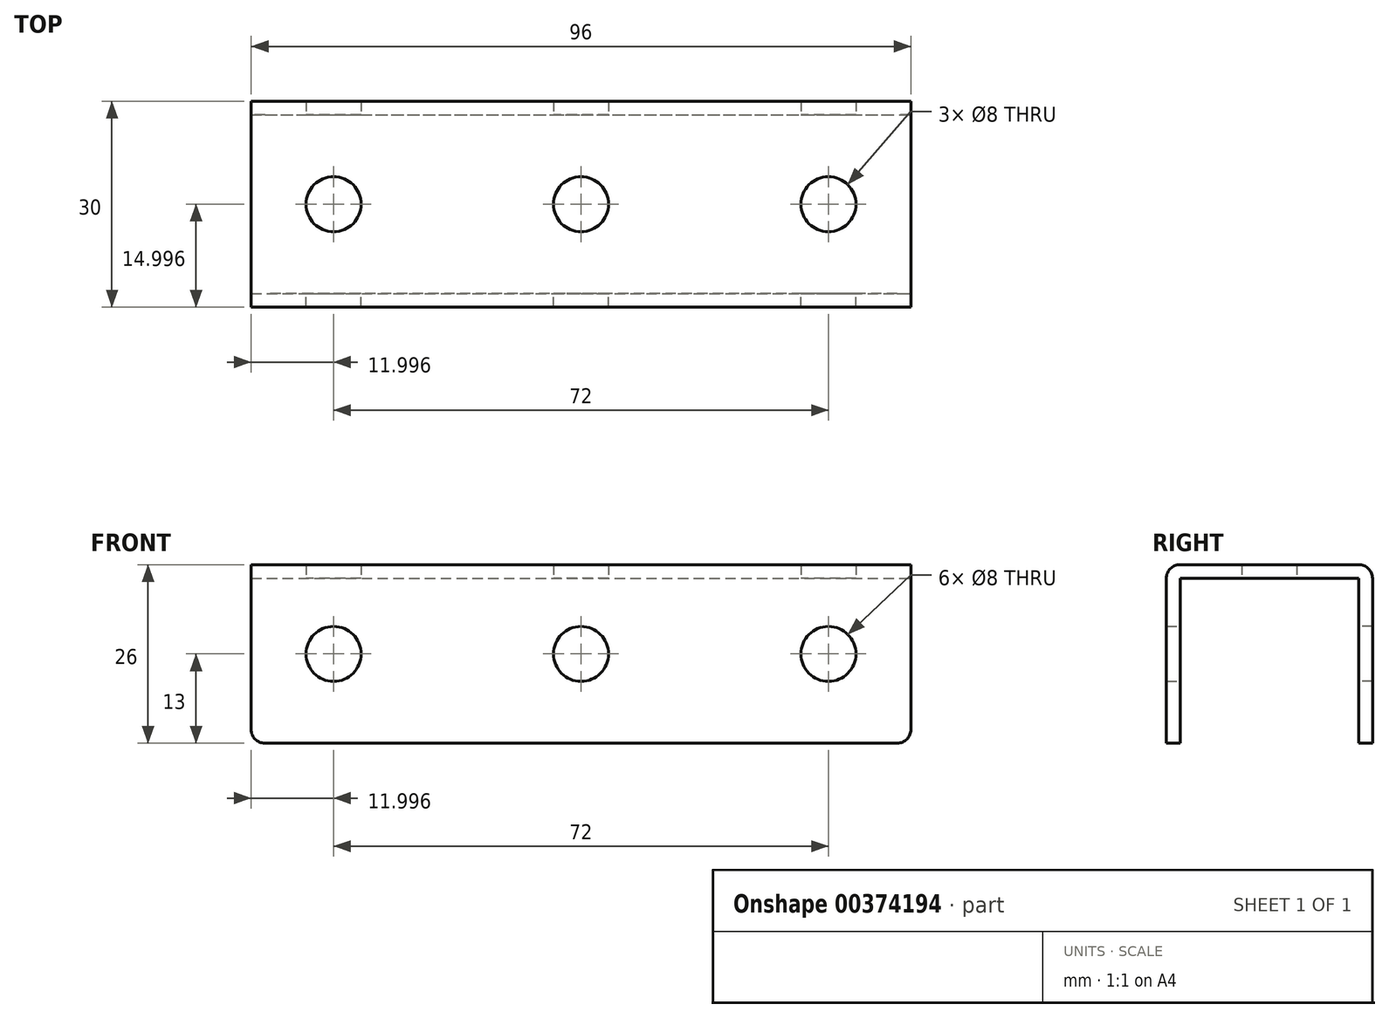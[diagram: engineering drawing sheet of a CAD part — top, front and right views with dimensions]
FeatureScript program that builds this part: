
annotation { "Feature Type Name" : "Feature", "Feature Type Description" : "" }
export const myFeature = defineFeature(function(context is Context, id is Id, definition is map)
    precondition{}
    {
        {
            var Q0;
            Q0=qCreatedBy(makeId("Top.planeOp"),FACE);
            var sketch = newSketch(context, id + "F0", { "sketchPlane" : qUnion([Q0])});
            skLineSegment(sketch, "E0.bottom", {"start": v(-30.68, 13.97) * mm, "end": v(65.32, 13.97) * mm});
            skLineSegment(sketch, "E0.top", {"start": v(-30.68, -12.03) * mm, "end": v(65.32, -12.03) * mm});
            skLineSegment(sketch, "E0.left", {"start": v(-30.68, 13.97) * mm, "end": v(-30.68, -12.03) * mm});
            skLineSegment(sketch, "E0.right", {"start": v(65.32, 13.97) * mm, "end": v(65.32, -12.03) * mm});
            skLineSegment(sketch, "E1", {"start": v(17.32, 13.97) * mm, "end": v(17.32, -12.03) * mm, "construction": true});
            skLineSegment(sketch, "E2", {"start": v(53.32, 13.97) * mm, "end": v(53.32, -12.03) * mm, "construction": true});
            skLineSegment(sketch, "E3", {"start": v(-18.68, 13.97) * mm, "end": v(-18.68, -12.03) * mm, "construction": true});
            skCircle(sketch, "E4", {"center": v(17.32, 0.97) * mm, "radius": 4 * mm});
            skCircle(sketch, "E5", {"center": v(53.32, 0.97) * mm, "radius": 4 * mm});
            skCircle(sketch, "E6", {"center": v(-18.68, 0.97) * mm, "radius": 4 * mm});
            skSolve(sketch);
        }
        {
            var Q0;
            Q0=makeQuery(id+"F0.imprint","IMPRINT",FACE,{"disambiguationData":[TD([[makeQuery(id+"F0.imprint","IMPRINT",EDGE,{"derivedFrom":sQuery(id+"F0.wireOp",EDGE,"E0.bottom")}),-1.0]])]});
            extrude(context, id + "F1", {"entities" : qUnion([Q0]), "depth" : 2 * mm});
        }
        {
            var Q0;
            Q0=makeQuery(id+"F1.opExtrude","SWEPT_FACE",FACE,{"disambiguationData":[OSD([sQuery(id+"F0.wireOp",EDGE,"E0.bottom")])]});
            cPlane(context, id + "F2", {"entities" : qUnion([Q0]), "cplaneType" : CPlaneType.OFFSET, "offset" : 0 * mm, "width" : 150 * mm, "height" : 150 * mm});
        }
        {
            var Q0;
            Q0=makeQuery(id+"F1.opExtrude","SWEPT_FACE",FACE,{"disambiguationData":[OSD([sQuery(id+"F0.wireOp",EDGE,"E0.top")])]});
            cPlane(context, id + "F3", {"entities" : qUnion([Q0]), "cplaneType" : CPlaneType.OFFSET, "offset" : 0 * mm, "width" : 150 * mm, "height" : 150 * mm});
        }
        {
            var Q0;
            Q0=qCreatedBy(id+"F2.planeOp",FACE);
            var sketch = newSketch(context, id + "F4", { "sketchPlane" : qUnion([Q0])});
            skLineSegment(sketch, "E7.0", {"start": v(30.68, 2) * mm, "end": v(-65.32, 2) * mm});
            skLineSegment(sketch, "E8", {"start": v(-65.32, 2) * mm, "end": v(-65.32, -24) * mm});
            skLineSegment(sketch, "E9", {"start": v(30.68, 2) * mm, "end": v(30.68, -24) * mm});
            skLineSegment(sketch, "E10", {"start": v(30.68, -24) * mm, "end": v(-65.32, -24) * mm});
            skLineSegment(sketch, "E11", {"start": v(-53.32, 2) * mm, "end": v(-53.32, -24) * mm, "construction": true});
            skLineSegment(sketch, "E12", {"start": v(18.68, 2) * mm, "end": v(18.68, -24) * mm, "construction": true});
            skLineSegment(sketch, "E13", {"start": v(-17.32, 2) * mm, "end": v(-17.32, -24) * mm, "construction": true});
            skCircle(sketch, "E14", {"center": v(-17.32, -11) * mm, "radius": 4 * mm});
            skCircle(sketch, "E15", {"center": v(18.68, -11) * mm, "radius": 4 * mm});
            skCircle(sketch, "E16", {"center": v(-53.32, -11) * mm, "radius": 4 * mm});
            skSolve(sketch);
        }
        {
            var Q0;
            Q0=qCreatedBy(id+"F3.planeOp",FACE);
            var sketch = newSketch(context, id + "F5", { "sketchPlane" : qUnion([Q0])});
            skLineSegment(sketch, "E17.0.0", {"start": v(65.32, -24) * mm, "end": v(-30.68, -24) * mm});
            skLineSegment(sketch, "E17.0.1", {"start": v(-30.68, -24) * mm, "end": v(-30.68, 2) * mm});
            skLineSegment(sketch, "E17.0.2", {"start": v(-30.68, 2) * mm, "end": v(65.32, 2) * mm});
            skLineSegment(sketch, "E17.0.3", {"start": v(65.32, 2) * mm, "end": v(65.32, -24) * mm});
            skCircle(sketch, "E18.0", {"center": v(-18.68, -11) * mm, "radius": 4 * mm});
            skCircle(sketch, "E19.0", {"center": v(17.32, -11) * mm, "radius": 4 * mm});
            skCircle(sketch, "E20.0", {"center": v(53.32, -11) * mm, "radius": 4 * mm});
            skSolve(sketch);
        }
        {
            var Q0;
            Q0=makeQuery(id+"F5.imprint","IMPRINT",FACE,{"disambiguationData":[TD([[makeQuery(id+"F5.imprint","IMPRINT",EDGE,{"derivedFrom":sQuery(id+"F5.wireOp",EDGE,"E17.0.0")}),-1.0]])]});
            extrude(context, id + "F6", {"entities" : qUnion([Q0]), "operationType" : NewBodyOperationType.ADD, "depth" : 2 * mm});
        }
        {
            var Q0;
            Q0=makeQuery(id+"F4.imprint","IMPRINT",FACE,{"disambiguationData":[TD([[makeQuery(id+"F4.imprint","IMPRINT",EDGE,{"derivedFrom":sQuery(id+"F4.wireOp",EDGE,"E7.0")}),1.0]])]});
            extrude(context, id + "F7", {"entities" : qUnion([Q0]), "operationType" : NewBodyOperationType.ADD, "depth" : 2 * mm});
        }
        {
            var Q0;
            Q0=makeQuery(id+"F6.opExtrude","CAP_EDGE",EDGE,{"disambiguationData":[OSD([sQuery(id+"F5.wireOp",EDGE,"E17.0.2")])],"isStart":false});
            var Q1;
            Q1=makeQuery(id+"F7.opExtrude","CAP_EDGE",EDGE,{"disambiguationData":[OSD([sQuery(id+"F4.wireOp",EDGE,"E7.0")])],"isStart":false});
            var Q2;
            Q2=makeQuery(id+"F7.opExtrude","SWEPT_EDGE",EDGE,{"disambiguationData":[OSD([sQuery(id+"F4.wireOp",EDGE,"E8"),sQuery(id+"F4.wireOp",EDGE,"E10")])]});
            var Q3;
            Q3=makeQuery(id+"F6.opExtrude","SWEPT_EDGE",EDGE,{"disambiguationData":[OSD([sQuery(id+"F5.wireOp",EDGE,"E17.0.0"),sQuery(id+"F5.wireOp",EDGE,"E17.0.3")])]});
            var Q4;
            Q4=makeQuery(id+"F7.opExtrude","SWEPT_EDGE",EDGE,{"disambiguationData":[OSD([sQuery(id+"F4.wireOp",EDGE,"E9"),sQuery(id+"F4.wireOp",EDGE,"E10")])]});
            var Q5;
            Q5=makeQuery(id+"F6.opExtrude","SWEPT_EDGE",EDGE,{"disambiguationData":[OSD([sQuery(id+"F5.wireOp",EDGE,"E17.0.0"),sQuery(id+"F5.wireOp",EDGE,"E17.0.1")])]});
            fillet(context, id + "F8", {"entities" : qUnion([Q0, Q1, Q2, Q3, Q4, Q5]), "radius" : 2 * mm, "tangentPropagation" : true, "allowEdgeOverflow" : false});
        }
    });
